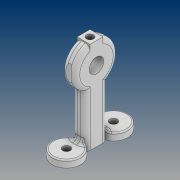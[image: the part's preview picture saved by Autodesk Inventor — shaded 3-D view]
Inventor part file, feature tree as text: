
AUTODESK INVENTOR PART (.ipt)
format: ipt  version: 2021 (Build 250183000, 183)  size: 321,536 bytes
history: native  units: mm
features: sketch x5, extrude x4, fillet x3, projected_geometry x2, hole x1, plane x1
ambient origin geometry x8: Origin, YZ Plane, XZ Plane, XY Plane, X Axis, Y Axis, Z Axis, Center Point
bodies: Solid1 (feature_tree)
feature tree (16):
  extrude  "Extrusion1"  Depth=12.0mm
  extrude  "Extrusion2"  Depth=3.0mm TaperAngle=0.0deg
  hole  "Hole1"  [1 undecoded]
  fillet  "Fillet1"  Radius=6.0mm
  plane  "Work Plane1"
  extrude  "Extrusion3"  Depth=2.0mm
  extrude  "Extrusion4"  Depth=5.5mm
  fillet  "Fillet2"  Radius=2.0mm
  fillet  "Fillet3"  Radius=3.0mm
  sketch  "Sketch1"  dims[d0=20.0mm d1=12.0mm]
  sketch  "Sketch2"  dims[d2=5.5mm d3=3.0mm d4=0.0mm]
  projected_geometry  "Projected Loop1"
  sketch  "Sketch3"  dims[d5=6.2mm d6=30.0mm d7=6.0mm]
  projected_geometry  "Projected Loop2"
  sketch  "Sketch4"  dims[d9=5.5mm d10=0.0mm]
  sketch  "Sketch5"  dims[d11=3.2mm d12=6.0mm d13=4.0mm d14=2.0mm d15=90.0deg d16=8.0mm d17=20.594885mm d18=2.0mm d19=5.5mm d21=2.0mm d22=0.0mm d23=3.0mm d24=7.75mm d25=0.0mm d26=2.0mm d27=0.5mm]
note: 1 required parameter value undecoded (feature->parameter linkage not recoverable at this tier; creation-order binding heuristic only, values carry confidence <= 0.55)
